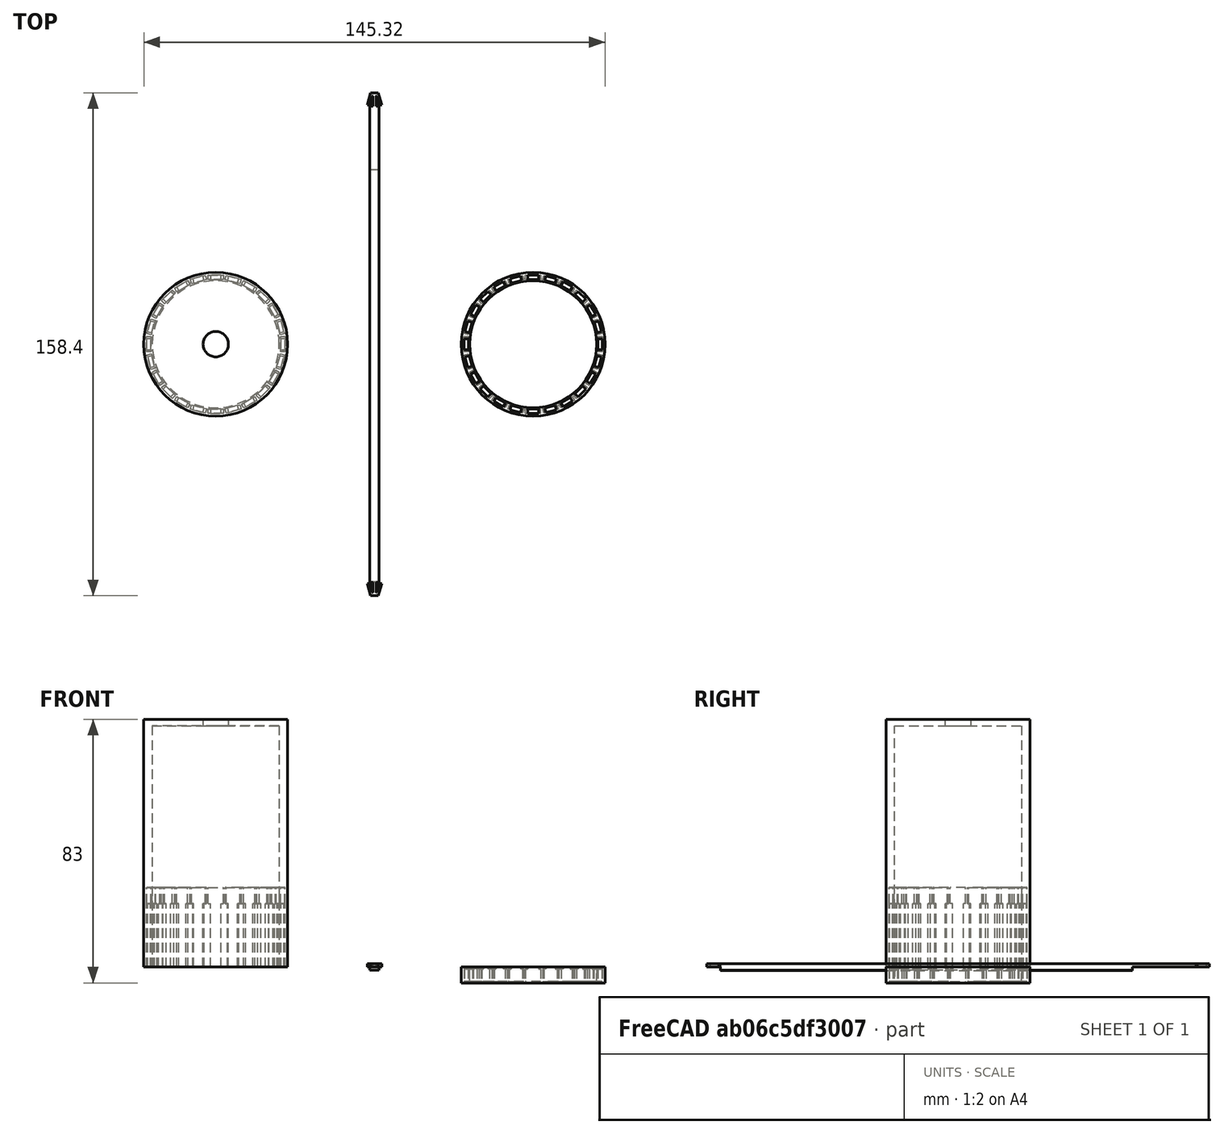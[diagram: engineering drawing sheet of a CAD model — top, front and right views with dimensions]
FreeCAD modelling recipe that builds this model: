
FCSTD DOCUMENT  (FreeCAD 1.0R38641 +468 (Git))
Label: SlenderLamp
License: All rights reserved
LicenseURL: http://en.wikipedia.org/wiki/All_rights_reserved
objects: App::Link×26, PartDesign::Pocket×5, Sketcher::SketchObject×4, PartDesign::Pad×4, PartDesign::Body×3, PartDesign::Mirrored×2, PartDesign::SubShapeBinder×2, PartDesign::PolarPattern×2, PartDesign::MultiTransform×1, Assembly::JointGroup×1, Assembly::AssemblyObject×1
note: 50 computed .brp shape members not serialized (recipe doc carries the construction recipe); baked Part::Feature solids carry a one-line shape summary decoded from their .brp

FEATURE [Sketcher::SketchObject] Sketch
  ArcFitTolerance = 1e-06
  AttachmentSupport = -> [XY_Plane]
  FullyConstrained = false
  MakeInternals = false
  MapMode = 5
  expr: Constraints[29] = 65 mm + 20 mm / 2
  sketch-geometry (11):
    g0: LineSegment StartX=0 StartY=0 StartZ=0 EndX=0 EndY=79.2 EndZ=0
    g1: LineSegment StartX=0 StartY=79.2 StartZ=0 EndX=1.237 EndY=79.2 EndZ=0
    g2: LineSegment StartX=0.5 StartY=78.1 StartZ=0 EndX=0.5 EndY=75 EndZ=0
    g3: LineSegment StartX=0 StartY=0 StartZ=0 EndX=1.5 EndY=0 EndZ=0
    g4: LineSegment StartX=0.5 StartY=75 StartZ=0 EndX=1.5 EndY=75 EndZ=0
    g5: LineSegment StartX=1.5 StartY=75 StartZ=0 EndX=1.5 EndY=0 EndZ=0
    g6: ArcOfCircle CenterX=0.6 CenterY=78.1 CenterZ=0 NormalX=0 NormalY=0 NormalZ=1 AngleXU=0 Radius=0.1 StartAngle=0.261799 EndAngle=3.14159
    g7: LineSegment StartX=2.27228 StartY=75.3363 StartZ=0 EndX=1.237 EndY=79.2 EndZ=0
    g8: LineSegment StartX=1.44406 StartY=75.3363 StartZ=0 EndX=0.696593 EndY=78.1259 EndZ=0
    g9: LineSegment [constr] StartX=0.359783 StartY=78.2 StartZ=0 EndX=1.0954 EndY=78.2 EndZ=0
    g10: LineSegment StartX=1.44406 StartY=75.3363 StartZ=0 EndX=2.27228 EndY=75.3363 EndZ=0
  constraints (30):
    c: Coincident(g0,g-1)
    c: Coincident(g3,g0)
    c: Horizontal(g1)
    c: PointOnObject(g3,g-1)
    c: Horizontal(g4)
    c: Coincident(g5,g4)
    c: Coincident(g5,g3)
    c: Vertical(g5)
    c: Distance(g3,g3) = 1.5
    c: Coincident(g2,g4)
    c: Distance(g4,g4) = 1
    c: Perpendicular(g2,g4)
    c: Coincident(g7,g1)
    c: Tangent(g8,g6) = -1.5708
    c: Tangent(g6,g2) = -1.5708
    c: Parallel(g8,g7)
    c: Diameter(g6) = 0.2
    c: Horizontal(g9)
    c: Tangent(g9,g6)
    c: Distance(g1,g9) = 1
    c: PointOnObject(g0,g-2)
    c: Coincident(g10,g8)
    c: Coincident(g10,g7)
    c: Coincident(g1,g0)
    c: DistanceY(g2,g0) = 4.2
    c: Distance(g7,g7) = 4
    c: Angle(g7,g10) = 1.309
    c: Horizontal(g10)
    c: Distance(g8,g7) = 0.8
    c: DistanceY(g5,g5) = 75
FEATURE [PartDesign::Pad] Pad
  Direction = (0,0,1)
  Length = 1
  Length2 = 10
  Profile = -> Sketch
  ReferenceAxis = -> Sketch [N_Axis]
  Refine = true
  Suppressed = false
  Type = 0
FEATURE [PartDesign::Mirrored] Mirrored
  MirrorPlane = -> Sketch [V_Axis]
  Refine = true
  Suppressed = false
  TransformMode = 0
FEATURE [PartDesign::Mirrored] Mirrored001
  MirrorPlane = -> Sketch [H_Axis]
  Refine = true
  Suppressed = false
  TransformMode = 0
FEATURE [PartDesign::MultiTransform] MultiTransform
  BaseFeature = -> Pad
  Originals = -> [Pad]
  Refine = true
  Suppressed = false
  TransformMode = 0
  Transformations = -> [Mirrored,Mirrored001]
FEATURE [Sketcher::SketchObject] Sketch001
  ArcFitTolerance = 1e-06
  AttachmentOffset = pos=(0,0,0) rot=(0,0,1;-1.5708rad)
  AttachmentSupport = -> [XY_Plane001]
  FullyConstrained = true
  MakeInternals = false
  MapMode = 5
  Placement = pos=(0,0,0) rot=(0,0,1;4.71239rad)
  sketch-geometry (13):
    g0: Circle CenterX=0 CenterY=0 CenterZ=0 NormalX=0 NormalY=0 NormalZ=1 AngleXU=0 Radius=20
    g1: Circle CenterX=0 CenterY=0 CenterZ=0 NormalX=0 NormalY=0 NormalZ=1 AngleXU=0 Radius=22.6638
    g2: LineSegment StartX=20.4 StartY=1.7 StartZ=0 EndX=20.4 EndY=-1.7 EndZ=0
    g3: LineSegment StartX=20.4 StartY=-1.7 StartZ=0 EndX=21.8 EndY=-1.7 EndZ=0
    g4: LineSegment StartX=21.8 StartY=-1.7 StartZ=0 EndX=21.8 EndY=1.7 EndZ=0
    g5: LineSegment StartX=21.8 StartY=1.7 StartZ=0 EndX=20.4 EndY=1.7 EndZ=0
    g6: LineSegment [constr] StartX=21.8 StartY=1.7 StartZ=0 EndX=22.6 EndY=1.7 EndZ=0
    g7: LineSegment StartX=20.4 StartY=1.7 StartZ=0 EndX=20.4 EndY=2.4 EndZ=0
    g8: LineSegment StartX=20.4 StartY=2.4 StartZ=0 EndX=21.8 EndY=2.4 EndZ=0
    g9: LineSegment StartX=21.8 StartY=2.4 StartZ=0 EndX=21.8 EndY=1.7 EndZ=0
    g10: LineSegment StartX=21.8 StartY=-1.7 StartZ=0 EndX=21.8 EndY=-2.4 EndZ=0
    g11: LineSegment StartX=21.8 StartY=-2.4 StartZ=0 EndX=20.4 EndY=-2.4 EndZ=0
    g12: LineSegment StartX=20.4 StartY=-2.4 StartZ=0 EndX=20.4 EndY=-1.7 EndZ=0
  constraints (34):
    c: Diameter(g0) = 40
    c: Coincident(g0,g-1)
    c: Coincident(g1,g0)
    c: Coincident(g2,g3)
    c: Coincident(g3,g4)
    c: Coincident(g4,g5)
    c: Coincident(g5,g2)
    c: Vertical(g4)
    c: Horizontal(g3)
    c: Horizontal(g5)
    c: Distance(g0,g2) = 0.4
    c: Coincident(g6,g4)
    c: PointOnObject(g6,g1)
    c: Horizontal(g6)
    c: Distance(g6,g6) = 0.8
    c: Distance(g3,g3) = 1.4
    c: Symmetric(g2,g2,g-1)
    c: DistanceY(g2,g2) = 3.4
    c: Coincident(g7,g2)
    c: Vertical(g7)
    c: Coincident(g8,g7)
    c: Horizontal(g8)
    c: Coincident(g9,g8)
    c: Coincident(g9,g4)
    c: Vertical(g9)
    c: Coincident(g10,g3)
    c: Vertical(g10)
    c: Coincident(g11,g10)
    c: Horizontal(g11)
    c: Coincident(g12,g11)
    c: Coincident(g12,g2)
    c: Vertical(g12)
    c: Equal(g12,g7)
    c: DistanceY(g11,g7) = 4.8
FEATURE [PartDesign::Pad] Pad001
  Direction = (0,0,1)
  Length = 5
  Length2 = 10
  Profile = -> Sketch001 [Edge1,Edge2]
  ReferenceAxis = -> Sketch001 [N_Axis]
  Refine = true
  Reversed = true
  Suppressed = false
  Type = 0
FEATURE [PartDesign::Pocket] Pocket
  BaseFeature = -> Pad001
  Direction = (0,0,-1)
  Length = 0
  Length2 = 5
  Offset = -0.4
  Profile = -> Sketch001 [Edge4,Edge3,Edge8,Edge9]
  ReferenceAxis = -> Sketch001 [N_Axis]
  Refine = true
  Suppressed = false
  Type = 3
  UpToFace = -> Pad001 [Face4]
FEATURE [PartDesign::SubShapeBinder] Binder
  BindCopyOnChange = 0
  BindMode = 0
  ClaimChildren = false
  Context = -> Body001 [Binder.]
  Fuse = false
  MakeFace = true
  OffsetFill = false
  OffsetIntersection = false
  OffsetJoinType = 0
  OffsetOpenResult = false
  PartialLoad = false
  Placement = pos=(0,0,-0.6) rot=(0,0,1;0rad)
  Refine = true
  Relative = true
  Support = -> [Sketch001[Edge5,Edge6,Edge7,Edge8,Edge3,Edge10,Edge11,Edge12]]
  _Version = 2
FEATURE [PartDesign::Pocket] Pocket001
  BaseFeature = -> Pocket
  Direction = (0,0,-1)
  Length = 0
  Length2 = 5
  Profile = -> Binder
  Refine = true
  Suppressed = false
  Type = 3
  UpToFace = -> Pocket [Face9]
FEATURE [PartDesign::PolarPattern] PolarPattern
  Angle = 360
  Axis = -> Sketch001 [N_Axis]
  BaseFeature = -> Pocket001
  Mode = 0
  Occurrences = 24
  Offset = 120
  Originals = -> [Pocket,Pocket001]
  Refine = true
  Suppressed = false
  TransformMode = 0
FEATURE [PartDesign::Body] Body001  label="Bottom"
  AllowCompound = false
  Group = -> [Sketch001,Pad001,Pocket,Binder,Pocket001,PolarPattern]
  Origin = -> Origin001
  Placement = pos=(250,0,0) rot=(0,0,1;0rad)
  Tip = -> PolarPattern
FEATURE [Assembly::JointGroup] Joints
FEATURE [App::Link] Collar  label="Collar001"
  LinkedObject = -> Body001
FEATURE [App::Link] Pillar  label="Pillar001"
  LinkPlacement = pos=(0,21.5,74.7) rot=(1,0,0;1.5708rad)
  LinkedObject = -> Body
  Placement = pos=(0,21.5,74.7) rot=(1,0,0;1.5708rad)
FEATURE [App::Link] Pillar001  label="Pillar002"
  LinkPlacement = pos=(-5.56461,20.7674,74.7) rot=(0.983106,0.129428,0.129428;1.58783rad)
  LinkedObject = -> Body
  Placement = pos=(-5.56461,20.7674,74.7) rot=(0.983106,0.129428,0.129428;1.58783rad)
FEATURE [App::Link] Pillar002  label="Pillar003"
  LinkPlacement = pos=(-10.75,18.6196,74.7) rot=(0.935113,0.250563,0.250563;1.63783rad)
  LinkedObject = -> Body
  Placement = pos=(-10.75,18.6196,74.7) rot=(0.935113,0.250563,0.250563;1.63783rad)
FEATURE [App::Link] Pillar003  label="Pillar004"
  LinkPlacement = pos=(-15.2028,15.2028,74.7) rot=(0.862856,0.357407,0.357407;1.71777rad)
  LinkedObject = -> Body
  Placement = pos=(-15.2028,15.2028,74.7) rot=(0.862856,0.357407,0.357407;1.71777rad)
FEATURE [App::Link] Pillar004  label="Pillar005"
  LinkPlacement = pos=(-18.6196,10.75,74.7) rot=(0.774597,0.447214,0.447214;1.82348rad)
  LinkedObject = -> Body
  Placement = pos=(-18.6196,10.75,74.7) rot=(0.774597,0.447214,0.447214;1.82348rad)
FEATURE [App::Link] Pillar005  label="Pillar006"
  LinkPlacement = pos=(-20.7674,5.56461,74.7) rot=(0.677661,0.519988,0.519988;1.95044rad)
  LinkedObject = -> Body
  Placement = pos=(-20.7674,5.56461,74.7) rot=(0.677661,0.519988,0.519988;1.95044rad)
FEATURE [App::Link] Pillar006  label="Pillar007"
  LinkPlacement = pos=(-21.5,-2.563e-06,74.7) rot=(0.57735,0.57735,0.57735;2.0944rad)
  LinkedObject = -> Body
  Placement = pos=(-21.5,-2.563e-06,74.7) rot=(0.57735,0.57735,0.57735;2.0944rad)
FEATURE [App::Link] Pillar007  label="Pillar008"
  LinkPlacement = pos=(-20.7674,-5.56461,74.7) rot=(0.476905,0.621515,0.621515;2.25159rad)
  LinkedObject = -> Body
  Placement = pos=(-20.7674,-5.56461,74.7) rot=(0.476905,0.621515,0.621515;2.25159rad)
FEATURE [App::Link] Pillar008  label="Pillar009"
  LinkPlacement = pos=(-18.6195,-10.75,74.7) rot=(0.377964,0.654654,0.654654;2.41886rad)
  LinkedObject = -> Body
  Placement = pos=(-18.6195,-10.75,74.7) rot=(0.377964,0.654654,0.654654;2.41886rad)
FEATURE [App::Link] Pillar009  label="Pillar010"
  LinkPlacement = pos=(-15.2028,-15.2028,74.7) rot=(0.281085,0.678598,0.678598;2.59356rad)
  LinkedObject = -> Body
  Placement = pos=(-15.2028,-15.2028,74.7) rot=(0.281085,0.678598,0.678598;2.59356rad)
FEATURE [App::Link] Pillar010  label="Pillar011"
  LinkPlacement = pos=(-10.75,-18.6195,74.7) rot=(0.186157,0.694747,0.694747;2.77349rad)
  LinkedObject = -> Body
  Placement = pos=(-10.75,-18.6195,74.7) rot=(0.186157,0.694747,0.694747;2.77349rad)
FEATURE [App::Link] Pillar011  label="Pillar012"
  LinkPlacement = pos=(-5.56461,-20.7674,74.7) rot=(0.092692,0.704063,0.704063;2.95674rad)
  LinkedObject = -> Body
  Placement = pos=(-5.56461,-20.7674,74.7) rot=(0.092692,0.704063,0.704063;2.95674rad)
FEATURE [App::Link] Pillar012  label="Pillar013"
  LinkPlacement = pos=(1.87959e-06,-21.5,74.7) rot=(0,0.707107,0.707107;3.14159rad)
  LinkedObject = -> Body
  Placement = pos=(1.87959e-06,-21.5,74.7) rot=(0,0.707107,0.707107;3.14159rad)
FEATURE [App::Link] Pillar013  label="Pillar014"
  LinkPlacement = pos=(5.56461,-20.7674,74.7) rot=(-0.092692,0.704063,0.704063;3.32645rad)
  LinkedObject = -> Body
  Placement = pos=(5.56461,-20.7674,74.7) rot=(-0.092692,0.704063,0.704063;3.32645rad)
FEATURE [App::Link] Pillar014  label="Pillar015"
  LinkPlacement = pos=(10.75,-18.6195,74.7) rot=(-0.186157,0.694747,0.694747;3.50969rad)
  LinkedObject = -> Body
  Placement = pos=(10.75,-18.6195,74.7) rot=(-0.186157,0.694747,0.694747;3.50969rad)
FEATURE [App::Link] Pillar015  label="Pillar016"
  LinkPlacement = pos=(15.2028,-15.2028,74.7) rot=(-0.281085,0.678598,0.678598;3.68962rad)
  LinkedObject = -> Body
  Placement = pos=(15.2028,-15.2028,74.7) rot=(-0.281085,0.678598,0.678598;3.68962rad)
FEATURE [App::Link] Pillar016  label="Pillar017"
  LinkPlacement = pos=(18.6195,-10.75,74.7) rot=(-0.377964,0.654654,0.654654;3.86433rad)
  LinkedObject = -> Body
  Placement = pos=(18.6195,-10.75,74.7) rot=(-0.377964,0.654654,0.654654;3.86433rad)
FEATURE [App::Link] Pillar017  label="Pillar018"
  LinkPlacement = pos=(20.7674,-5.56461,74.7) rot=(-0.476905,0.621515,0.621515;4.0316rad)
  LinkedObject = -> Body
  Placement = pos=(20.7674,-5.56461,74.7) rot=(-0.476905,0.621515,0.621515;4.0316rad)
FEATURE [App::Link] Pillar018  label="Pillar019"
  LinkPlacement = pos=(21.5,-2.563e-06,74.7) rot=(-0.57735,0.57735,0.57735;4.18879rad)
  LinkedObject = -> Body
  Placement = pos=(21.5,-2.563e-06,74.7) rot=(-0.57735,0.57735,0.57735;4.18879rad)
FEATURE [App::Link] Pillar019  label="Pillar020"
  LinkPlacement = pos=(20.7674,5.56461,74.7) rot=(0.677661,-0.519988,-0.519988;1.95044rad)
  LinkedObject = -> Body
  Placement = pos=(20.7674,5.56461,74.7) rot=(0.677661,-0.519988,-0.519988;1.95044rad)
FEATURE [App::Link] Pillar020  label="Pillar021"
  LinkPlacement = pos=(18.6195,10.75,74.7) rot=(0.774597,-0.447213,-0.447214;1.82348rad)
  LinkedObject = -> Body
  Placement = pos=(18.6195,10.75,74.7) rot=(0.774597,-0.447213,-0.447214;1.82348rad)
FEATURE [App::Link] Pillar021  label="Pillar022"
  LinkPlacement = pos=(15.2028,15.2028,74.7) rot=(0.862856,-0.357407,-0.357407;1.71777rad)
  LinkedObject = -> Body
  Placement = pos=(15.2028,15.2028,74.7) rot=(0.862856,-0.357407,-0.357407;1.71777rad)
FEATURE [App::Link] Pillar022  label="Pillar023"
  LinkPlacement = pos=(10.75,18.6196,74.7) rot=(0.935113,-0.250563,-0.250563;1.63783rad)
  LinkedObject = -> Body
  Placement = pos=(10.75,18.6196,74.7) rot=(0.935113,-0.250563,-0.250563;1.63783rad)
FEATURE [App::Link] Pillar023  label="Pillar024"
  LinkPlacement = pos=(5.56461,20.7674,74.7) rot=(0.983106,-0.129428,-0.129428;1.58783rad)
  LinkedObject = -> Body
  Placement = pos=(5.56461,20.7674,74.7) rot=(0.983106,-0.129428,-0.129428;1.58783rad)
FEATURE [Sketcher::SketchObject] Sketch002
  ArcFitTolerance = 1e-06
  AttachmentOffset = pos=(0,0,0) rot=(0,0,1;-1.5708rad)
  FullyConstrained = true
  MakeInternals = false
  MapMode = 5
  Placement = pos=(0,0,0) rot=(0,0,1;4.71239rad)
  sketch-geometry (14):
    g0: Circle CenterX=0 CenterY=0 CenterZ=0 NormalX=0 NormalY=0 NormalZ=1 AngleXU=0 Radius=20
    g1: Circle CenterX=0 CenterY=0 CenterZ=0 NormalX=0 NormalY=0 NormalZ=1 AngleXU=0 Radius=22.6638
    g2: LineSegment StartX=20.4 StartY=1.7 StartZ=0 EndX=20.4 EndY=-1.7 EndZ=0
    g3: LineSegment StartX=20.4 StartY=-1.7 StartZ=0 EndX=21.8 EndY=-1.7 EndZ=0
    g4: LineSegment StartX=21.8 StartY=-1.7 StartZ=0 EndX=21.8 EndY=1.7 EndZ=0
    g5: LineSegment StartX=21.8 StartY=1.7 StartZ=0 EndX=20.4 EndY=1.7 EndZ=0
    g6: LineSegment [constr] StartX=21.8 StartY=1.7 StartZ=0 EndX=22.6 EndY=1.7 EndZ=0
    g7: LineSegment StartX=20.4 StartY=1.7 StartZ=0 EndX=20.4 EndY=2.4 EndZ=0
    g8: LineSegment StartX=20.4 StartY=2.4 StartZ=0 EndX=21.8 EndY=2.4 EndZ=0
    g9: LineSegment StartX=21.8 StartY=2.4 StartZ=0 EndX=21.8 EndY=1.7 EndZ=0
    g10: LineSegment StartX=21.8 StartY=-1.7 StartZ=0 EndX=21.8 EndY=-2.4 EndZ=0
    g11: LineSegment StartX=21.8 StartY=-2.4 StartZ=0 EndX=20.4 EndY=-2.4 EndZ=0
    g12: LineSegment StartX=20.4 StartY=-2.4 StartZ=0 EndX=20.4 EndY=-1.7 EndZ=0
    g13: Circle CenterX=0 CenterY=0 CenterZ=0 NormalX=0 NormalY=0 NormalZ=1 AngleXU=0 Radius=4
  constraints (36):
    c: Diameter(g0) = 40
    c: Coincident(g0,g-1)
    c: Coincident(g1,g0)
    c: Coincident(g2,g3)
    c: Coincident(g3,g4)
    c: Coincident(g4,g5)
    c: Coincident(g5,g2)
    c: Vertical(g4)
    c: Horizontal(g3)
    c: Horizontal(g5)
    c: Distance(g0,g2) = 0.4
    c: Coincident(g6,g4)
    c: PointOnObject(g6,g1)
    c: Horizontal(g6)
    c: Distance(g6,g6) = 0.8
    c: Distance(g3,g3) = 1.4
    c: Symmetric(g2,g2,g-1)
    c: DistanceY(g2,g2) = 3.4
    c: Coincident(g7,g2)
    c: Vertical(g7)
    c: Coincident(g8,g7)
    c: Horizontal(g8)
    c: Coincident(g9,g8)
    c: Coincident(g9,g4)
    c: Vertical(g9)
    c: Coincident(g10,g3)
    c: Vertical(g10)
    c: Coincident(g11,g10)
    c: Horizontal(g11)
    c: Coincident(g12,g11)
    c: Coincident(g12,g2)
    c: Vertical(g12)
    c: Equal(g12,g7)
    c: DistanceY(g11,g7) = 4.8
    c: Diameter(g13) = 8
    c: Coincident(g13,g0)
FEATURE [PartDesign::Pad] Pad002
  Direction = (0,0,1)
  Length = 78
  Length2 = 10
  Placement = pos=(0,0,0) rot=(0,0,1;4.71239rad)
  Profile = -> Sketch002 [Edge2,Edge13]
  ReferenceAxis = -> Sketch002 [N_Axis]
  Refine = true
  Suppressed = false
  Type = 0
FEATURE [PartDesign::Pocket] Pocket002
  BaseFeature = -> Pad002
  Direction = (0,0,-1)
  Length = 0
  Length2 = 5
  Offset = -2
  Placement = pos=(0,0,0) rot=(0,0,1;4.71239rad)
  Profile = -> Sketch002 [Edge1]
  ReferenceAxis = -> Sketch002 [N_Axis]
  Refine = true
  Suppressed = false
  Type = 3
  UpToFace = -> Pad002 [Face4]
FEATURE [PartDesign::SubShapeBinder] Binder001
  BindCopyOnChange = 0
  BindMode = 0
  ClaimChildren = false
  Context = -> Body002 [Binder001.]
  Fuse = false
  MakeFace = true
  OffsetFill = false
  OffsetIntersection = false
  OffsetJoinType = 0
  OffsetOpenResult = false
  PartialLoad = false
  Placement = pos=(0,0,20) rot=(0,0,1;0rad)
  Refine = true
  Relative = true
  Support = -> [Sketch002[Edge11,Edge12,Edge10,Edge3,Edge8,Edge7,Edge5,Edge6]]
  _Version = 2
FEATURE [PartDesign::Pocket] Pocket003
  BaseFeature = -> Pocket002
  Direction = (0,0,-1)
  Length = 20
  Length2 = 5
  Placement = pos=(0,0,0) rot=(0,0,1;4.71239rad)
  Profile = -> Sketch002 [Edge3,Edge4,Edge8,Edge9]
  ReferenceAxis = -> Sketch002 [N_Axis]
  Refine = true
  Reversed = true
  Suppressed = false
  Type = 0
FEATURE [PartDesign::Pocket] Pocket004
  BaseFeature = -> Pocket003
  Direction = (0,0,-1)
  Length = 5
  Length2 = 5
  Placement = pos=(0,0,0) rot=(0,0,1;4.71239rad)
  Profile = -> Binder001
  Refine = true
  Reversed = true
  Suppressed = false
  Type = 0
FEATURE [PartDesign::PolarPattern] PolarPattern001
  Angle = 360
  Axis = -> Sketch002 [N_Axis]
  BaseFeature = -> Pocket004
  Mode = 0
  Occurrences = 24
  Offset = 120
  Originals = -> [Pocket003,Pocket004]
  Placement = pos=(0,0,0) rot=(0,0,1;4.71239rad)
  Refine = true
  Suppressed = false
  TransformMode = 0
FEATURE [PartDesign::Body] Body002  label="Top"
  AllowCompound = false
  Group = -> [Sketch002,Pad002,Pocket002,Binder001,Pocket003,Pocket004,PolarPattern001]
  Origin = -> Origin003
  Placement = pos=(150,0,0) rot=(0,0,1;0rad)
  Tip = -> PolarPattern001
FEATURE [App::Link] Top  label="Top001"
  LinkPlacement = pos=(0,-1.54991e-05,130) rot=(0,0,1;0rad)
  LinkedObject = -> Body002
  Placement = pos=(0,-1.54991e-05,130) rot=(0,0,1;0rad)
FEATURE [Assembly::AssemblyObject] Assembly
  Group = -> [Joints,Collar,Pillar,Pillar001,Pillar002,Pillar003,Pillar004,Pillar005,Pillar006,Pillar007,Pillar008,Pillar009,Pillar010,Pillar011,Pillar012,Pillar013,Pillar014,Pillar015,Pillar016,Pillar017,Pillar018,Pillar019,Pillar020,Pillar021,Pillar022,Pillar023,Top]
  Origin = -> Origin002
  Type = Assembly
FEATURE [Sketcher::SketchObject] Sketch003
  ArcFitTolerance = 1e-06
  AttachmentSupport = -> [XZ_Plane]
  ExternalGeometry = -> [MultiTransform]
  FullyConstrained = true
  MakeInternals = false
  MapMode = 5
  Placement = pos=(0,0,0) rot=(1,0,0;1.5708rad)
  sketch-geometry (4):
    g0: ArcOfCircle CenterX=0 CenterY=21.6103 CenterZ=0 NormalX=0 NormalY=0 NormalZ=1 AngleXU=0 Radius=22.66 StartAngle=4.64614 EndAngle=4.77863
    g1: LineSegment StartX=1.5 StartY=-1 StartZ=0 EndX=1.5 EndY=0 EndZ=0
    g2: LineSegment StartX=-1.5 StartY=0 StartZ=0 EndX=-1.5 EndY=-1 EndZ=0
    g3: LineSegment StartX=-1.5 StartY=0 StartZ=0 EndX=1.5 EndY=0 EndZ=0
  constraints (13):
    c: PointOnObject(g0,g-2)
    c: Coincident(g1,g0)
    c: PointOnObject(g1,g-1)
    c: PointOnObject(g2,g-1)
    c: PointOnObject(g2,g-5)
    c: PointOnObject(g1,g-6)
    c: Coincident(g2,g0)
    c: PointOnObject(g0,g-5)
    c: PointOnObject(g0,g-6)
    c: Radius(g0) = 22.66
    c: Distance(g2) = 1
    c: Coincident(g3,g2)
    c: Coincident(g3,g1)
FEATURE [PartDesign::Pad] Pad003
  BaseFeature = -> MultiTransform
  Direction = (0,-1,2e-16)
  Length = 74.8
  Length2 = 55
  Profile = -> Sketch003
  ReferenceAxis = -> Sketch003 [N_Axis]
  Refine = true
  Suppressed = false
  Type = 4
FEATURE [PartDesign::Body] Body  label="Connector"
  AllowCompound = false
  Group = -> [Sketch,Pad,MultiTransform,Mirrored,Mirrored001,Sketch003,Pad003]
  Origin = -> Origin
  Placement = pos=(200,0,0) rot=(1,0,0;0rad)
  Tip = -> Pad003
